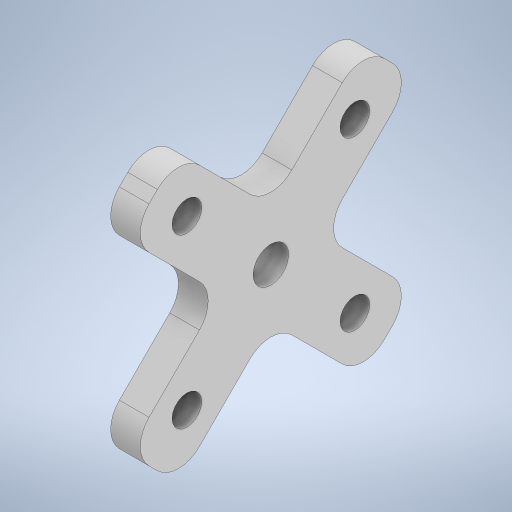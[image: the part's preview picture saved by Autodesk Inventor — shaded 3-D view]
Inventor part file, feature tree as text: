
AUTODESK INVENTOR PART (.ipt)
format: ipt  version: 2023 (Build 270158000, 158)  size: 304,640 bytes
history: native  units: in
note: dims shown in document units (in); Inventor stores cm internally (conversion verified against a paired STEP export)
features: extrude x1, fillet x1, sketch x1
ambient origin geometry x8: Origin, YZ Plane, XZ Plane, XY Plane, X Axis, Y Axis, Z Axis, Center Point
bodies: Solid1 (feature_tree)
feature tree (3):
  extrude  "Extrusion1"  Depth=1.414in
  fillet  "Fillet1"  Radius=0.3in
  sketch  "Sketch1"  dims[d0=1.414in d1=1.414in d2=0.3in d3=0.25in d4=0.25in d5=0.25in d6=0.25in d7=0.3in d8=1.4in d9=0.6in d10=1.4in d11=0.6in d12=1.4in d13=0.25in d14=0.0in d15=0.25in]
